# Revit family: QF_ELECTROLUXPROFESSIONAL_1LSNLE_IC64825R
name_source: partatom
category: Specialty Equipment
revit_build: Autodesk Revit 2018 (Build: 20190510_1515(x64)
units: mm (PartAtom-declared; Revit-internal decimal feet)

## family parameters
Always vertical = Yes
Cut with Voids When Loaded = No
Part Type = Normal
Room Calculation Point = No
Round Connector Dimension = Use Diameter
Shared = No
Work Plane-Based = No

## types (1)
- QF_ELECTROLUXPROFESSIONAL_1LSNLE_IC64825R
    -B/2 = -1270 mm  [stored -4.16667 ft]
    A_Width = 3205 mm  [stored 10.5151 ft]
    B_2 = 1270 mm  [stored 4.16667 ft]
    B_IronerWidth = 2540 mm
    C_WithBetweenFeet = 2930 mm  [stored 9.61286 ft]
    DepthMax = 1100 mm
    DepthPedestal = 950 mm  [stored 3.1168 ft]
    Feet = 80 mm  [stored 0.262467 ft]
    Height = 1270 mm  [stored 4.16667 ft]

note: [stored X ft] marks values corroborated as IEEE doubles in the binary element streams (Revit-internal decimal feet)

## geometry (parser evidence)
native form markers: Sweep x8
no freeform markers — native parametric forms only
